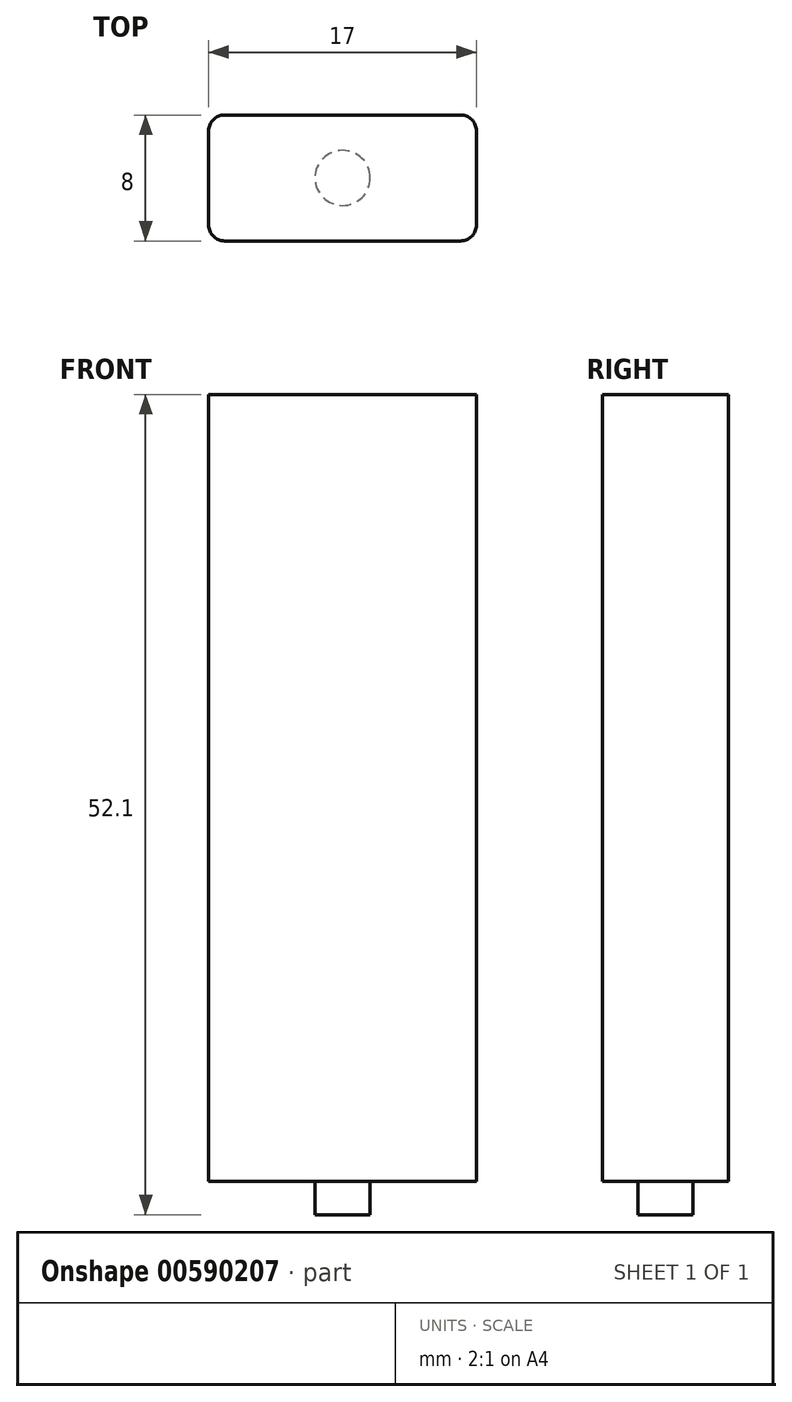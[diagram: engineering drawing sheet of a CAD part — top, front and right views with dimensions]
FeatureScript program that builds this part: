
annotation { "Feature Type Name" : "Feature", "Feature Type Description" : "" }
export const myFeature = defineFeature(function(context is Context, id is Id, definition is map)
    precondition{}
    {
        {
            var Q0;
            Q0=qCreatedBy(makeId("Top.planeOp"),FACE);
            var sketch = newSketch(context, id + "F0", { "sketchPlane" : qUnion([Q0])});
            skLineSegment(sketch, "E0.bottom", {"start": v(-8.5, 4) * mm, "end": v(8.5, 4) * mm});
            skLineSegment(sketch, "E0.top", {"start": v(-8.5, -4) * mm, "end": v(8.5, -4) * mm});
            skLineSegment(sketch, "E0.left", {"start": v(-8.5, 4) * mm, "end": v(-8.5, -4) * mm});
            skLineSegment(sketch, "E0.right", {"start": v(8.5, 4) * mm, "end": v(8.5, -4) * mm});
            skPoint(sketch, "E0.middle", {"position": v(0, 0) * mm});
            skSolve(sketch);
        }
        {
            var Q0;
            Q0 = qSketchRegion(id + "F0", true);
            extrude(context, id + "F1", {"entities" : qUnion([Q0]), "depth" : 50 * mm, "offsetDistance" : 25 * mm});
        }
        {
            var Q0;
            Q0=makeQuery(id+"F1.opExtrude","CAP_FACE",FACE,{"disambiguationData":[OSD([sQuery(id+"F0.wireOp",EDGE,"E0.bottom"),sQuery(id+"F0.wireOp",EDGE,"E0.top"),sQuery(id+"F0.wireOp",EDGE,"E0.left"),sQuery(id+"F0.wireOp",EDGE,"E0.right")])],"isStart":true});
            var sketch = newSketch(context, id + "F2", { "sketchPlane" : qUnion([Q0])});
            skCircle(sketch, "E1", {"center": v(0, 0) * mm, "radius": 1.75 * mm});
            skSolve(sketch);
        }
        {
            var Q0;
            Q0 = qSketchRegion(id + "F2", true);
            extrude(context, id + "F3", {"entities" : qUnion([Q0]), "operationType" : NewBodyOperationType.ADD, "depth" : 2.1 * mm, "offsetDistance" : 25 * mm});
        }
        {
            var Q0;
            Q0=makeQuery(id+"F1.opExtrude","SWEPT_EDGE",EDGE,{"disambiguationData":[OSD([sQuery(id+"F0.wireOp",EDGE,"E0.bottom"),sQuery(id+"F0.wireOp",EDGE,"E0.left")])]});
            var Q1;
            Q1=makeQuery(id+"F1.opExtrude","SWEPT_EDGE",EDGE,{"disambiguationData":[OSD([sQuery(id+"F0.wireOp",EDGE,"E0.bottom"),sQuery(id+"F0.wireOp",EDGE,"E0.right")])]});
            var Q2;
            Q2=makeQuery(id+"F1.opExtrude","SWEPT_EDGE",EDGE,{"disambiguationData":[OSD([sQuery(id+"F0.wireOp",EDGE,"E0.top"),sQuery(id+"F0.wireOp",EDGE,"E0.right")])]});
            var Q3;
            Q3=makeQuery(id+"F1.opExtrude","SWEPT_EDGE",EDGE,{"disambiguationData":[OSD([sQuery(id+"F0.wireOp",EDGE,"E0.top"),sQuery(id+"F0.wireOp",EDGE,"E0.left")])]});
            fillet(context, id + "F4", {"entities" : qUnion([Q0, Q1, Q2, Q3]), "radius" : 1 * mm, "tangentPropagation" : true, "allowEdgeOverflow" : false});
        }
    });
